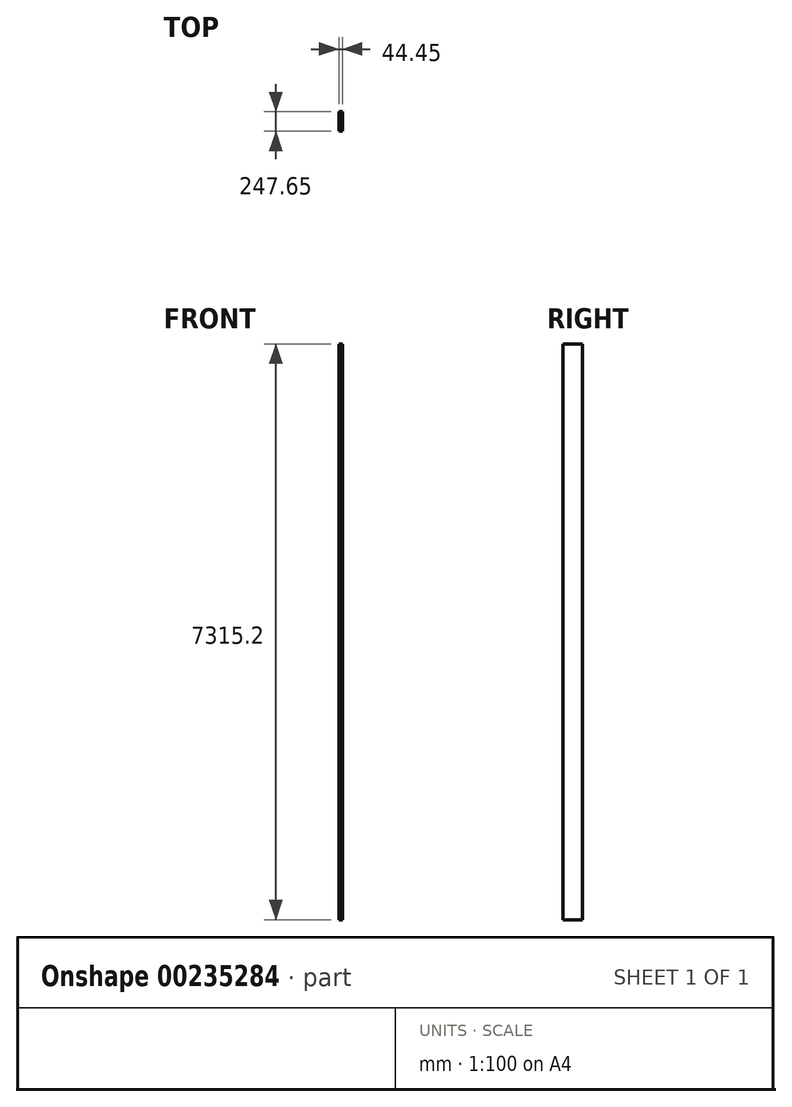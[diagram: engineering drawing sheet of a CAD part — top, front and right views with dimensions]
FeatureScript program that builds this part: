
annotation { "Feature Type Name" : "Feature", "Feature Type Description" : "" }
export const myFeature = defineFeature(function(context is Context, id is Id, definition is map)
    precondition{}
    {
        {
            var Q0;
            Q0=qCreatedBy(makeId("Top.planeOp"),FACE);
            var sketch = newSketch(context, id + "F0", { "sketchPlane" : qUnion([Q0])});
            skLineSegment(sketch, "E0", {"start": v(0, 0) * mm, "end": v(44.45, 0) * mm});
            skLineSegment(sketch, "E1", {"start": v(44.45, 0) * mm, "end": v(44.45, 247.65) * mm});
            skLineSegment(sketch, "E2", {"start": v(44.45, 247.65) * mm, "end": v(0, 247.65) * mm});
            skLineSegment(sketch, "E3", {"start": v(0, 247.65) * mm, "end": v(0, 0) * mm});
            skSolve(sketch);
        }
        {
            var Q0;
            Q0=makeQuery(id+"F0.imprint","IMPRINT",FACE,{"disambiguationData":[TD([[makeQuery(id+"F0.imprint","IMPRINT",EDGE,{"derivedFrom":sQuery(id+"F0.wireOp",EDGE,"E0")}),1.0]])]});
            extrude(context, id + "F1", {"entities" : qUnion([Q0]), "depth" : 7315.2 * mm});
        }
    });
